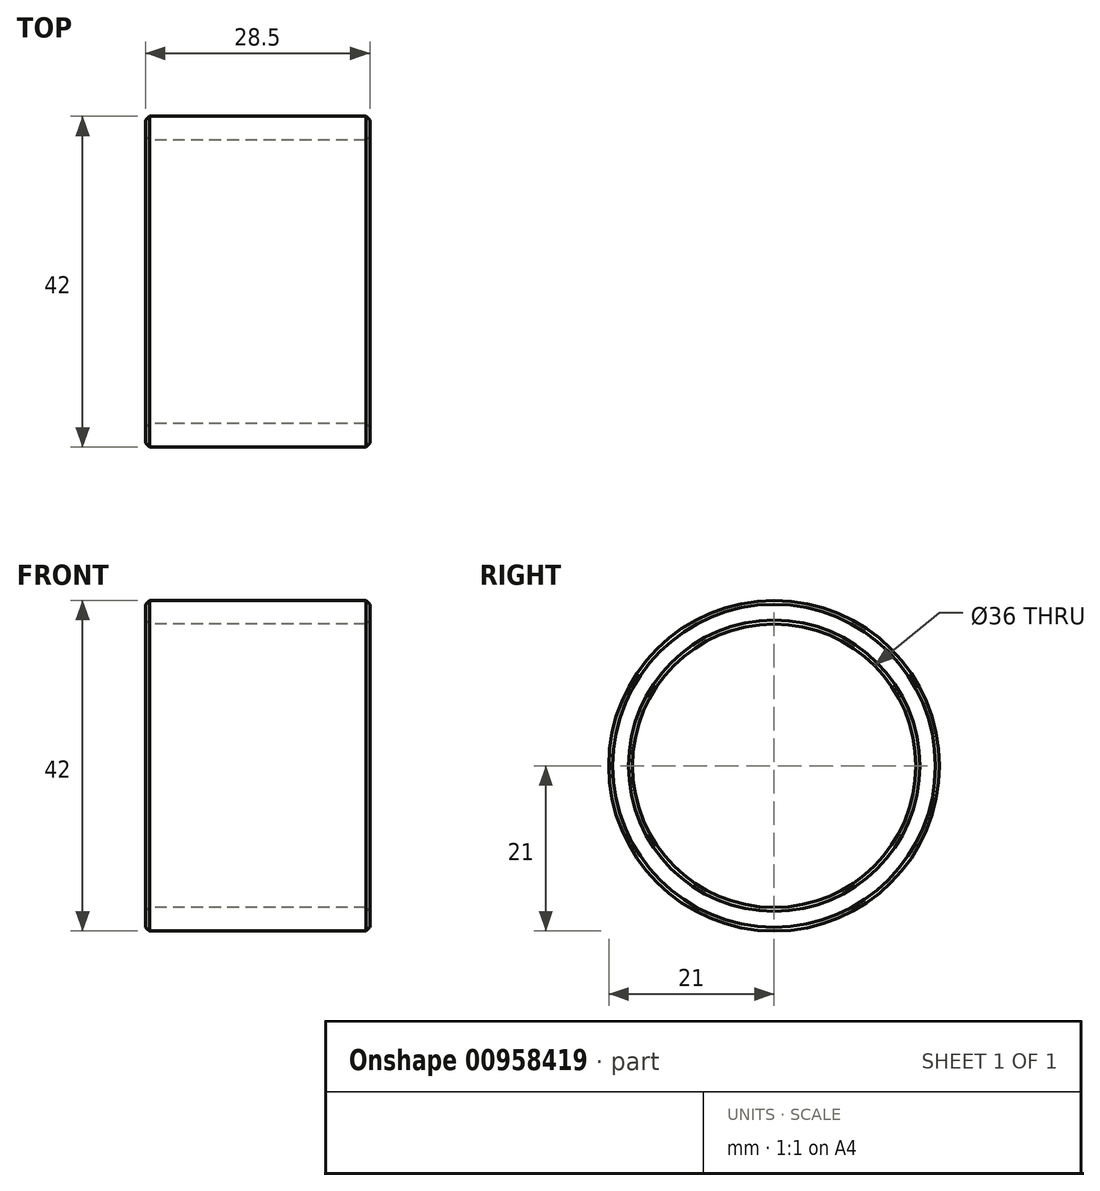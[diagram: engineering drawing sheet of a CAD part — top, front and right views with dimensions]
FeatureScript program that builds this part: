
annotation { "Feature Type Name" : "Feature", "Feature Type Description" : "" }
export const myFeature = defineFeature(function(context is Context, id is Id, definition is map)
    precondition{}
    {
        {
            var Q0;
            Q0=qCreatedBy(makeId("Front.planeOp"),FACE);
            var sketch = newSketch(context, id + "F0", { "sketchPlane" : qUnion([Q0])});
            skLineSegment(sketch, "E0.bottom", {"start": v(-6.2, 21) * mm, "end": v(22.3, 21) * mm});
            skLineSegment(sketch, "E0.top", {"start": v(-6.2, 18) * mm, "end": v(22.3, 18) * mm});
            skLineSegment(sketch, "E0.left", {"start": v(-6.2, 21) * mm, "end": v(-6.2, 18) * mm});
            skLineSegment(sketch, "E0.right", {"start": v(22.3, 21) * mm, "end": v(22.3, 18) * mm});
            skLineSegment(sketch, "E1", {"start": v(0, 0) * mm, "end": v(8.45, 0) * mm});
            skSolve(sketch);
        }
        {
            var Q0;
            Q0=qSketchRegion(id+"F0",true);
            var Q1;
            Q1=sQuery(id+"F0.wireOp",EDGE,"E1");
            revolve(context, id + "F1", {"surfaceOperationType" : NewSurfaceOperationType.NEW, "entities" : qUnion([Q0]), "axis" : qUnion([Q1]), "revolveType" : RevolveType.FULL});
        }
        {
            var Q0;
            Q0=makeQuery(id+"F1.opRevolve","SWEPT_FACE",FACE,{"disambiguationData":[OSD([sQuery(id+"F0.wireOp",EDGE,"E0.bottom")])]});
            var Q1;
            Q1=makeQuery(id+"F1.opRevolve","SWEPT_FACE",FACE,{"disambiguationData":[OSD([sQuery(id+"F0.wireOp",EDGE,"E0.top")])]});
            chamfer(context, id + "F2", {"entities" : qUnion([Q0, Q1]), "width" : 0.5 * mm, "tangentPropagation" : true});
        }
    });
